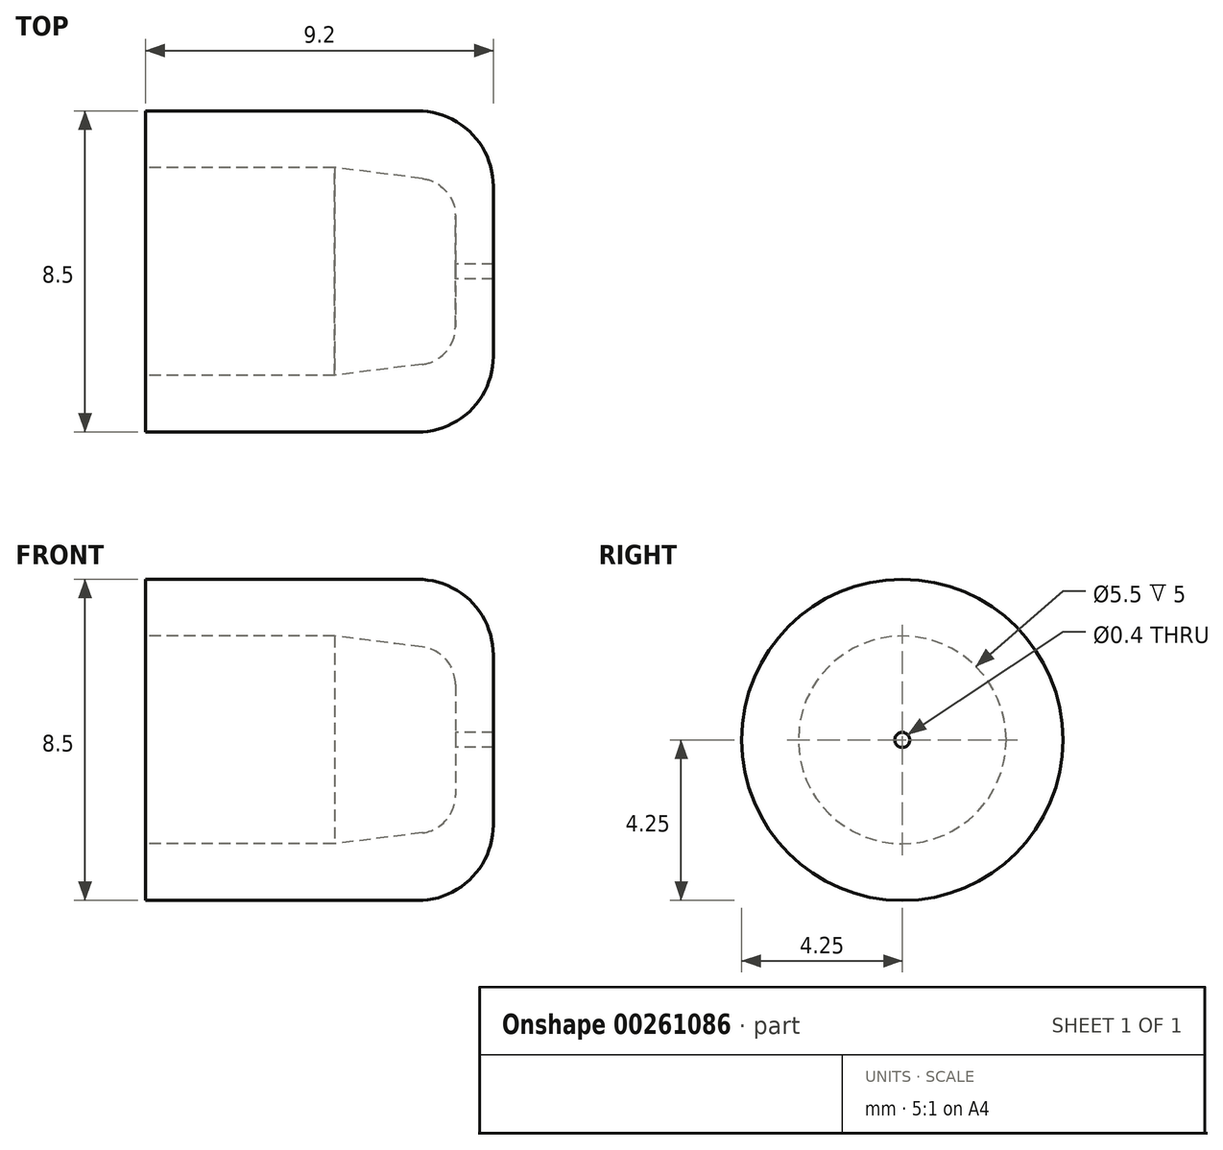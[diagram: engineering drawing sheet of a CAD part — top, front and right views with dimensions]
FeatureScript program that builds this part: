
annotation { "Feature Type Name" : "Feature", "Feature Type Description" : "" }
export const myFeature = defineFeature(function(context is Context, id is Id, definition is map)
    precondition{}
    {
        {
            var Q0;
            Q0=qCreatedBy(makeId("Top.planeOp"),FACE);
            var sketch = newSketch(context, id + "F0", { "sketchPlane" : qUnion([Q0])});
            skLineSegment(sketch, "E0", {"start": v(-6.23, 0) * mm, "end": v(9.94, 0) * mm, "construction": true});
            skLineSegment(sketch, "E1", {"start": v(-0.99, 2.75) * mm, "end": v(6.01, 2.75) * mm, "construction": true});
            skLineSegment(sketch, "E2", {"start": v(6.01, 2.75) * mm, "end": v(9.01, 2.35) * mm, "construction": true});
            skLineSegment(sketch, "E3", {"start": v(9.01, 2.35) * mm, "end": v(9.01, 1.96) * mm, "construction": true});
            skLineSegment(sketch, "E4", {"start": v(9.01, 1.96) * mm, "end": v(-0.99, 1.96) * mm, "construction": true});
            skLineSegment(sketch, "E5", {"start": v(-0.99, 1.96) * mm, "end": v(-0.99, 2.75) * mm, "construction": true});
            skLineSegment(sketch, "E6.2", {"start": v(-0.99, 4.25) * mm, "end": v(7.06, 4.25) * mm});
            skLineSegment(sketch, "E7", {"start": v(-0.99, 4.25) * mm, "end": v(-0.99, 2.75) * mm});
            skLineSegment(sketch, "E8", {"start": v(-0.99, 2.75) * mm, "end": v(5.35, 2.75) * mm});
            skLineSegment(sketch, "E9", {"start": v(7.45, 2.56) * mm, "end": v(6.67, 2.66) * mm});
            skLineSegment(sketch, "E10", {"start": v(9.01, 0.77) * mm, "end": v(9.01, 0.1) * mm});
            skLineSegment(sketch, "E11", {"start": v(9.01, 0.1) * mm, "end": v(10.01, 0.1) * mm});
            skLineSegment(sketch, "E12", {"start": v(10.01, 0.1) * mm, "end": v(10.01, 2.63) * mm});
            skLineSegment(sketch, "E13", {"start": v(8.38, 4.16) * mm, "end": v(8.71, 4.12) * mm});
            skPoint(sketch, "E14.visualSharp", {"position": v(6.01, 2.75) * mm});
            skArc(sketch, "E14.filletArc", {"start": v(6.67, 2.66) * mm, "mid": v(6.01, 2.73) * mm, "end": v(5.35, 2.75) * mm});
            skPoint(sketch, "E15.visualSharp", {"position": v(9.01, 2.35) * mm});
            skArc(sketch, "E15.filletArc", {"start": v(9.01, 0.77) * mm, "mid": v(8.57, 1.96) * mm, "end": v(7.45, 2.56) * mm});
            skPoint(sketch, "E16.visualSharp", {"position": v(7.72, 4.25) * mm});
            skArc(sketch, "E16.filletArc", {"start": v(8.38, 4.16) * mm, "mid": v(7.72, 4.23) * mm, "end": v(7.06, 4.25) * mm});
            skPoint(sketch, "E17.visualSharp", {"position": v(10.01, 3.94) * mm});
            skArc(sketch, "E17.filletArc", {"start": v(10.01, 2.63) * mm, "mid": v(9.64, 3.62) * mm, "end": v(8.71, 4.12) * mm});
            skSolve(sketch);
        }
        {
            var Q0;
            Q0=makeQuery(id+"F0.imprint","IMPRINT",FACE,{"disambiguationData":[TD([[makeQuery(id+"F0.imprint","IMPRINT",EDGE,{"derivedFrom":sQuery(id+"F0.wireOp",EDGE,"E6.2")}),-1.0]])]});
            var sketch = newSketch(context, id + "F1", { "sketchPlane" : qUnion([Q0])});
            skLineSegment(sketch, "E18", {"start": v(-1.63, 0) * mm, "end": v(6.73, 0) * mm, "construction": true});
            skLineSegment(sketch, "E19", {"start": v(0, -2.75) * mm, "end": v(5, -2.75) * mm, "construction": true});
            skLineSegment(sketch, "E20", {"start": v(5, -2.75) * mm, "end": v(8.2, -2.35) * mm, "construction": true});
            skLineSegment(sketch, "E21", {"start": v(8.2, -2.35) * mm, "end": v(8.2, -2.05) * mm, "construction": true});
            skLineSegment(sketch, "E22", {"start": v(8.2, -2.05) * mm, "end": v(0, -2.05) * mm, "construction": true});
            skLineSegment(sketch, "E23", {"start": v(0, -2.05) * mm, "end": v(0, -2.75) * mm, "construction": true});
            skLineSegment(sketch, "E24", {"start": v(0, -2.75) * mm, "end": v(5, -2.75) * mm});
            skLineSegment(sketch, "E25", {"start": v(8.2, -1.47) * mm, "end": v(8.2, -0.2) * mm});
            skLineSegment(sketch, "E26", {"start": v(8.2, -0.2) * mm, "end": v(9.2, -0.2) * mm});
            skLineSegment(sketch, "E27", {"start": v(9.2, -0.2) * mm, "end": v(9.2, -2.25) * mm});
            skLineSegment(sketch, "E28", {"start": v(0, -2.75) * mm, "end": v(0, -4.25) * mm});
            skLineSegment(sketch, "E29", {"start": v(0, -4.25) * mm, "end": v(7.2, -4.25) * mm});
            skLineSegment(sketch, "E30", {"start": v(5, -2.75) * mm, "end": v(7.32, -2.46) * mm});
            skPoint(sketch, "E31.visualSharp", {"position": v(8.2, -2.35) * mm});
            skArc(sketch, "E31.filletArc", {"start": v(7.32, -2.46) * mm, "mid": v(7.95, -2.13) * mm, "end": v(8.2, -1.47) * mm});
            skPoint(sketch, "E32.visualSharp", {"position": v(5, -2.75) * mm});
            skPoint(sketch, "E33.visualSharp", {"position": v(9.2, -4.25) * mm});
            skArc(sketch, "E33.filletArc", {"start": v(7.2, -4.25) * mm, "mid": v(8.61, -3.66) * mm, "end": v(9.2, -2.25) * mm});
            skSolve(sketch);
        }
        {
            var Q0;
            Q0=qCreatedBy(makeId("Top.planeOp"),FACE);
            var sketch = newSketch(context, id + "F2", { "sketchPlane" : qUnion([Q0])});
            skLineSegment(sketch, "E34", {"start": v(0, 0) * mm, "end": v(10.81, 0) * mm, "construction": true});
            skSolve(sketch);
        }
        {
            var Q0;
            Q0=makeQuery(id+"F1.imprint","IMPRINT",FACE,{"disambiguationData":[TD([[makeQuery(id+"F1.imprint","IMPRINT",EDGE,{"derivedFrom":sQuery(id+"F1.wireOp",EDGE,"E24")}),-1.0]])]});
            var Q1;
            Q1=sQuery(id+"F2.wireOp",EDGE,"E34");
            revolve(context, id + "F3", {"entities" : qUnion([Q0]), "axis" : qUnion([Q1]), "revolveType" : RevolveType.FULL});
        }
    });
